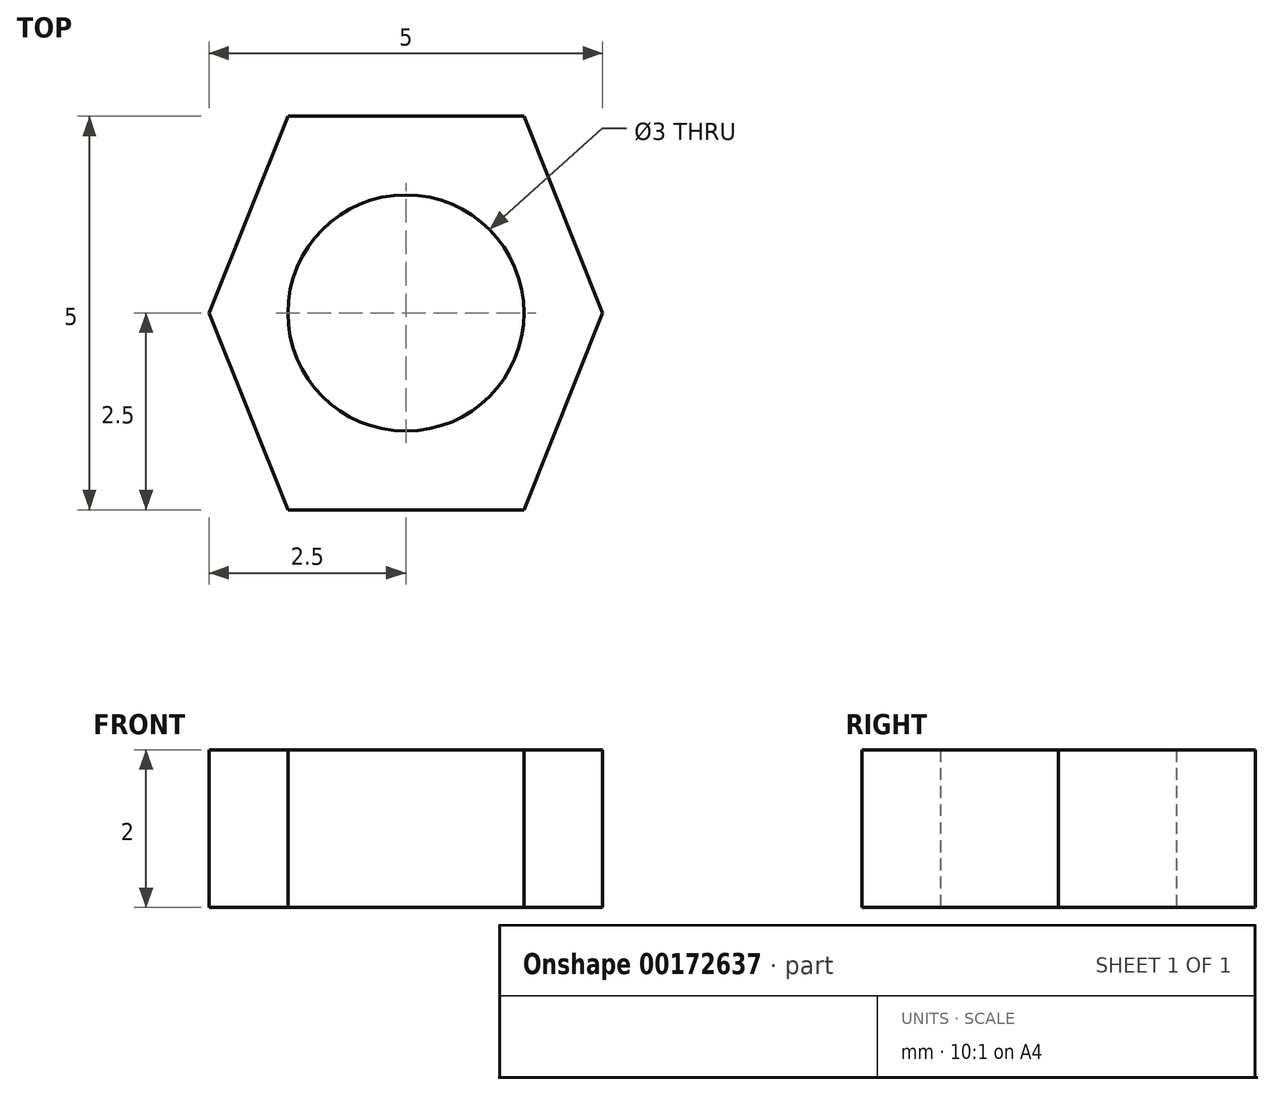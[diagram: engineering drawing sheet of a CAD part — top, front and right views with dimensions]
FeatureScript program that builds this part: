
annotation { "Feature Type Name" : "Feature", "Feature Type Description" : "" }
export const myFeature = defineFeature(function(context is Context, id is Id, definition is map)
    precondition{}
    {
        {
            var Q0;
            Q0=qCreatedBy(makeId("Top.planeOp"),FACE);
            var sketch = newSketch(context, id + "F0", { "sketchPlane" : qUnion([Q0])});
            skCircle(sketch, "E0", {"center": v(0, 0) * mm, "radius": 1.5 * mm});
            skLineSegment(sketch, "E1.bottom", {"start": v(-1.5, 2.5) * mm, "end": v(1.5, 2.5) * mm});
            skLineSegment(sketch, "E1.top", {"start": v(-1.5, -2.5) * mm, "end": v(1.5, -2.5) * mm});
            skPoint(sketch, "E2", {"position": v(-2.5, 0) * mm});
            skPoint(sketch, "E3", {"position": v(2.5, 0) * mm});
            skLineSegment(sketch, "E4", {"start": v(-2.5, 0) * mm, "end": v(-1.5, 2.5) * mm});
            skLineSegment(sketch, "E5", {"start": v(-2.5, 0) * mm, "end": v(-1.5, -2.5) * mm});
            skLineSegment(sketch, "E6", {"start": v(1.5, -2.5) * mm, "end": v(2.5, 0) * mm});
            skLineSegment(sketch, "E7", {"start": v(2.5, 0) * mm, "end": v(1.5, 2.5) * mm});
            skSolve(sketch);
        }
        {
            var Q0;
            Q0 = qSketchRegion(id + "F0", true);
            extrude(context, id + "F1", {"entities" : qUnion([Q0]), "depth" : 2 * mm});
        }
    });
